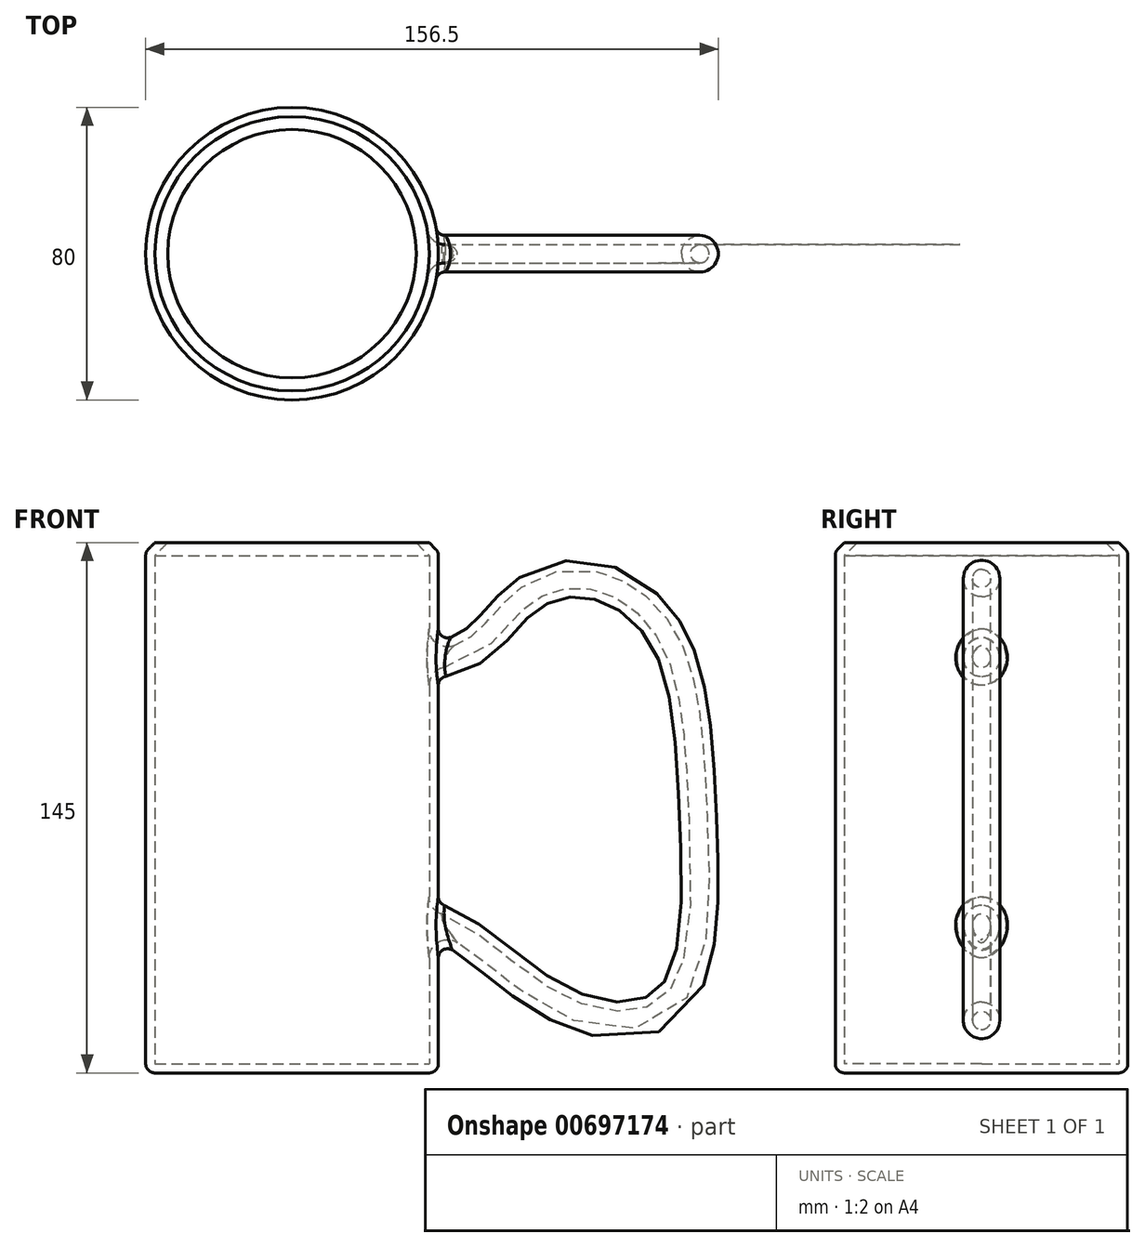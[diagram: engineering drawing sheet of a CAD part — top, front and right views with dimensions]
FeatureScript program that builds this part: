
annotation { "Feature Type Name" : "Feature", "Feature Type Description" : "" }
export const myFeature = defineFeature(function(context is Context, id is Id, definition is map)
    precondition{}
    {
        {
            var Q0;
            Q0=qCreatedBy(makeId("Top.planeOp"),FACE);
            var sketch = newSketch(context, id + "F0", { "sketchPlane" : qUnion([Q0])});
            skCircle(sketch, "E0", {"center": v(0, 0) * mm, "radius": 40 * mm});
            skSolve(sketch);
        }
        {
            var Q0;
            Q0 = qSketchRegion(id + "F0", true);
            extrude(context, id + "F1", {"entities" : qUnion([Q0]), "depth" : 145 * mm, "offsetDistance" : 25 * mm});
        }
        {
            var Q0;
            Q0=qCreatedBy(makeId("Front.planeOp"),FACE);
            var sketch = newSketch(context, id + "F2", { "sketchPlane" : qUnion([Q0])});
            skFitSpline(sketch, "E1", {"points": [v(24.67, 111.77) * mm, v(48.93, 115.63) * mm, v(64.37, 130.24) * mm, v(82.83, 134.1) * mm, v(102.4, 118.66) * mm, v(110.4, 70.42) * mm, v(103.78, 20.25) * mm, v(75.4, 18.32) * mm, v(43.14, 40.38) * mm, v(25.22, 43.13) * mm], "startDerivative": vector(263.18, 0.16) * mm, "endDerivative": vector(-198.7, -6.86) * mm});
            skSolve(sketch);
        }
        {
            var Q0;
            Q0=qCreatedBy(makeId("Right.planeOp"),FACE);
            cPlane(context, id + "F3", {"entities" : qUnion([Q0]), "cplaneType" : CPlaneType.OFFSET, "offset" : 24.8 * mm, "width" : 150 * mm, "height" : 150 * mm});
        }
        {
            var Q0;
            Q0=qCreatedBy(id+"F3.planeOp",FACE);
            var sketch = newSketch(context, id + "F4", { "sketchPlane" : qUnion([Q0])});
            skCircle(sketch, "E2", {"center": v(0, 112.32) * mm, "radius": 5 * mm});
            skSolve(sketch);
        }
        {
            var Q0;
            Q0 = qSketchRegion(id + "F4", true);
            var Q1;
            Q1 = qConstructionFilter(qBodyType(qCreatedBy(id + "F2" ,EDGE), BodyType.WIRE), ConstructionObject.NO);
            sweep(context, id + "F5", {"operationType" : NewBodyOperationType.ADD, "profiles" : qUnion([Q0]), "path" : qUnion([Q1])});
        }
        {
            var Q0;
            Q0=makeQuery(id+"F1.opExtrude","CAP_EDGE",EDGE,{"disambiguationData":[OSD([sQuery(id+"F0.wireOp",EDGE,"E0")])],"isStart":false});
            chamfer(context, id + "F6", {"entities" : qUnion([Q0]), "width" : 2.5 * mm, "tangentPropagation" : true});
        }
        {
            var Q0;
            Q0=makeQuery(id+"F1.opExtrude","CAP_EDGE",EDGE,{"disambiguationData":[OSD([sQuery(id+"F0.wireOp",EDGE,"E0")])],"isStart":true});
            var Q1;
            Q1=makeQuery(id+"F1.opExtrude","SWEPT_FACE",FACE,{"disambiguationData":[OSD([sQuery(id+"F0.wireOp",EDGE,"E0")])]});
            fillet(context, id + "F7", {"entities" : qUnion([Q0, Q1]), "radius" : 2.5 * mm, "tangentPropagation" : true, "allowEdgeOverflow" : false});
        }
        {
            var Q0;
            Q0=makeQuery(id+"F1.opExtrude","CAP_FACE",FACE,{"disambiguationData":[OSD([sQuery(id+"F0.wireOp",EDGE,"E0")])],"isStart":false});
            shell(context, id + "F8", {"entities" : qUnion([Q0]), "thickness" : 2.5 * mm});
        }
    });
